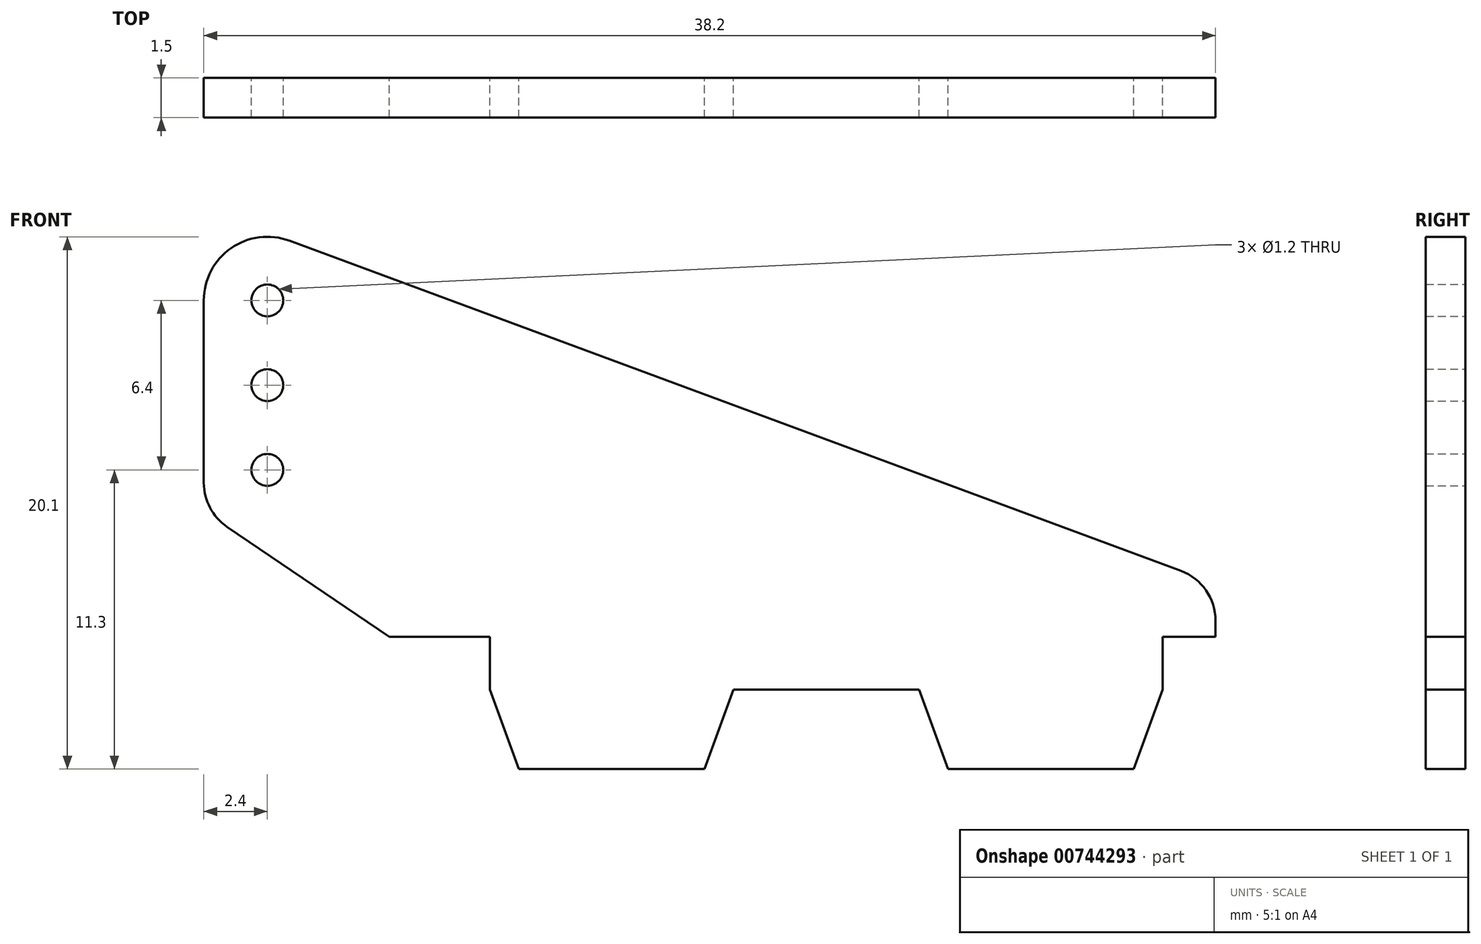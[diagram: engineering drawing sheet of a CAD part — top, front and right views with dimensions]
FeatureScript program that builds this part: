
annotation { "Feature Type Name" : "Feature", "Feature Type Description" : "" }
export const myFeature = defineFeature(function(context is Context, id is Id, definition is map)
    precondition{}
    {
        {
            var Q0;
            Q0=qCreatedBy(makeId("Front.planeOp"),FACE);
            var sketch = newSketch(context, id + "F0", { "sketchPlane" : qUnion([Q0])});
            skLineSegment(sketch, "E0", {"start": v(0, 0) * mm, "end": v(3.8, 0) * mm});
            skLineSegment(sketch, "E1", {"start": v(3.8, 0) * mm, "end": v(3.8, -2) * mm});
            skLineSegment(sketch, "E2", {"start": v(3.8, -2) * mm, "end": v(4.9, -5) * mm});
            skLineSegment(sketch, "E3", {"start": v(4.9, -5) * mm, "end": v(11.9, -5) * mm});
            skLineSegment(sketch, "E4", {"start": v(11.9, -5) * mm, "end": v(13, -2) * mm});
            skLineSegment(sketch, "E5", {"start": v(13, -2) * mm, "end": v(20, -2) * mm});
            skLineSegment(sketch, "E6", {"start": v(20, -2) * mm, "end": v(21.1, -5) * mm});
            skLineSegment(sketch, "E7", {"start": v(21.1, -5) * mm, "end": v(28.1, -5) * mm});
            skLineSegment(sketch, "E8", {"start": v(28.1, -5) * mm, "end": v(29.2, -2) * mm});
            skLineSegment(sketch, "E9", {"start": v(29.2, -2) * mm, "end": v(29.2, 0) * mm});
            skLineSegment(sketch, "E10", {"start": v(29.2, 0) * mm, "end": v(31.2, 0) * mm});
            skLineSegment(sketch, "E11", {"start": v(31.2, 0) * mm, "end": v(31.2, 0.6) * mm});
            skLineSegment(sketch, "E12", {"start": v(29.9, 2.48) * mm, "end": v(-3.77, 14.95) * mm});
            skLineSegment(sketch, "E13", {"start": v(0, 0) * mm, "end": v(-6.12, 4.15) * mm});
            skLineSegment(sketch, "E14", {"start": v(-7, 5.8) * mm, "end": v(-7, 12.7) * mm});
            skArc(sketch, "E15", {"start": v(-7, 12.7) * mm, "mid": v(-5.97, 14.67) * mm, "end": v(-3.77, 14.95) * mm});
            skCircle(sketch, "E16", {"center": v(-4.6, 12.7) * mm, "radius": 0.6 * mm});
            skPoint(sketch, "E17.visualSharp", {"position": v(31.2, 2) * mm});
            skArc(sketch, "E17.filletArc", {"start": v(31.2, 0.6) * mm, "mid": v(30.84, 1.75) * mm, "end": v(29.9, 2.48) * mm});
            skPoint(sketch, "E18.visualSharp", {"position": v(-7, 4.75) * mm});
            skArc(sketch, "E18.filletArc", {"start": v(-7, 5.8) * mm, "mid": v(-6.77, 4.87) * mm, "end": v(-6.12, 4.15) * mm});
            skCircle(sketch, "E19.0.1.0", {"center": v(-4.6, 9.5) * mm, "radius": 0.6 * mm});
            skCircle(sketch, "E19.0.2.0", {"center": v(-4.6, 6.3) * mm, "radius": 0.6 * mm});
            skLineSegment(sketch, "E19.direction1", {"start": v(-4.6, 12.7) * mm, "end": v(-29.6, 12.7) * mm, "construction": true});
            skLineSegment(sketch, "E19.direction2", {"start": v(-4.6, 12.7) * mm, "end": v(-4.6, 9.5) * mm, "construction": true});
            skLineSegment(sketch, "E20", {"start": v(26.13, 17.43) * mm, "end": v(22.33, 17.43) * mm});
            skLineSegment(sketch, "E21", {"start": v(22.33, 17.43) * mm, "end": v(22.33, 19.43) * mm});
            skLineSegment(sketch, "E22", {"start": v(22.33, 19.43) * mm, "end": v(21.24, 22.43) * mm});
            skLineSegment(sketch, "E23", {"start": v(21.24, 22.43) * mm, "end": v(14.23, 22.43) * mm});
            skLineSegment(sketch, "E24", {"start": v(14.23, 22.43) * mm, "end": v(13.13, 19.43) * mm});
            skLineSegment(sketch, "E25", {"start": v(13.13, 19.43) * mm, "end": v(6.12, 19.43) * mm});
            skLineSegment(sketch, "E26", {"start": v(6.12, 19.43) * mm, "end": v(5.03, 22.43) * mm});
            skLineSegment(sketch, "E27", {"start": v(5.03, 22.43) * mm, "end": v(-1.98, 22.43) * mm});
            skLineSegment(sketch, "E28", {"start": v(-1.98, 22.43) * mm, "end": v(-3.07, 19.43) * mm});
            skLineSegment(sketch, "E29", {"start": v(-3.07, 19.43) * mm, "end": v(-3.07, 17.43) * mm});
            skLineSegment(sketch, "E30", {"start": v(-3.07, 17.43) * mm, "end": v(-5.07, 17.43) * mm});
            skLineSegment(sketch, "E31", {"start": v(-5.07, 17.43) * mm, "end": v(-5.07, 16.83) * mm});
            skLineSegment(sketch, "E32", {"start": v(-3.77, 14.95) * mm, "end": v(29.9, 2.48) * mm});
            skLineSegment(sketch, "E33", {"start": v(26.13, 17.43) * mm, "end": v(32.25, 13.28) * mm});
            skLineSegment(sketch, "E34", {"start": v(33.13, 11.62) * mm, "end": v(33.13, 4.73) * mm});
            skArc(sketch, "E35", {"start": v(33.13, 4.73) * mm, "mid": v(32.1, 2.76) * mm, "end": v(29.9, 2.48) * mm});
            skCircle(sketch, "E36", {"center": v(30.73, 4.73) * mm, "radius": 0.6 * mm});
            skPoint(sketch, "E37.visualSharp", {"position": v(-5.07, 15.43) * mm});
            skArc(sketch, "E37.filletArc", {"start": v(-5.07, 16.83) * mm, "mid": v(-4.71, 15.68) * mm, "end": v(-3.77, 14.95) * mm});
            skPoint(sketch, "E38.visualSharp", {"position": v(33.13, 12.68) * mm});
            skArc(sketch, "E38.filletArc", {"start": v(33.13, 11.62) * mm, "mid": v(32.9, 12.56) * mm, "end": v(32.25, 13.28) * mm});
            skCircle(sketch, "E39.0.1.0", {"center": v(30.73, 7.93) * mm, "radius": 0.6 * mm});
            skCircle(sketch, "E39.0.2.0", {"center": v(30.73, 11.13) * mm, "radius": 0.6 * mm});
            skLineSegment(sketch, "E39.direction1", {"start": v(30.73, 4.73) * mm, "end": v(55.73, 4.73) * mm, "construction": true});
            skLineSegment(sketch, "E39.direction2", {"start": v(30.73, 4.73) * mm, "end": v(30.73, 7.93) * mm, "construction": true});
            skLineSegment(sketch, "E40", {"start": v(40.13, 0) * mm, "end": v(43.93, 0) * mm});
            skLineSegment(sketch, "E41", {"start": v(43.93, 0) * mm, "end": v(43.93, -2) * mm});
            skLineSegment(sketch, "E42", {"start": v(43.93, -2) * mm, "end": v(45.02, -5) * mm});
            skLineSegment(sketch, "E43", {"start": v(45.02, -5) * mm, "end": v(52.03, -5) * mm});
            skLineSegment(sketch, "E44", {"start": v(52.03, -5) * mm, "end": v(53.12, -2) * mm});
            skLineSegment(sketch, "E45", {"start": v(53.12, -2) * mm, "end": v(60.13, -2) * mm});
            skLineSegment(sketch, "E46", {"start": v(60.13, -2) * mm, "end": v(61.23, -5) * mm});
            skLineSegment(sketch, "E47", {"start": v(61.23, -5) * mm, "end": v(68.24, -5) * mm});
            skLineSegment(sketch, "E48", {"start": v(68.24, -5) * mm, "end": v(69.33, -2) * mm});
            skLineSegment(sketch, "E49", {"start": v(69.33, -2) * mm, "end": v(69.33, 0) * mm});
            skLineSegment(sketch, "E50", {"start": v(69.33, 0) * mm, "end": v(71.33, 0) * mm});
            skLineSegment(sketch, "E51", {"start": v(71.33, 0) * mm, "end": v(71.33, 0.6) * mm});
            skLineSegment(sketch, "E52", {"start": v(70.02, 2.48) * mm, "end": v(36.36, 14.95) * mm});
            skLineSegment(sketch, "E53", {"start": v(40.13, 0) * mm, "end": v(34, 4.15) * mm});
            skLineSegment(sketch, "E54", {"start": v(33.13, 5.8) * mm, "end": v(33.13, 12.7) * mm});
            skArc(sketch, "E55", {"start": v(33.13, 12.7) * mm, "mid": v(34.16, 14.67) * mm, "end": v(36.36, 14.95) * mm});
            skCircle(sketch, "E56", {"center": v(35.53, 12.7) * mm, "radius": 0.6 * mm});
            skPoint(sketch, "E57.visualSharp", {"position": v(71.33, 2) * mm});
            skArc(sketch, "E57.filletArc", {"start": v(71.33, 0.6) * mm, "mid": v(70.97, 1.75) * mm, "end": v(70.02, 2.48) * mm});
            skPoint(sketch, "E58.visualSharp", {"position": v(33.13, 4.75) * mm});
            skArc(sketch, "E58.filletArc", {"start": v(33.13, 5.8) * mm, "mid": v(33.36, 4.87) * mm, "end": v(34, 4.15) * mm});
            skCircle(sketch, "E59.0.1.0", {"center": v(35.53, 9.5) * mm, "radius": 0.6 * mm});
            skCircle(sketch, "E59.0.2.0", {"center": v(35.53, 6.3) * mm, "radius": 0.6 * mm});
            skLineSegment(sketch, "E59.direction1", {"start": v(35.53, 12.7) * mm, "end": v(10.53, 12.7) * mm, "construction": true});
            skLineSegment(sketch, "E59.direction2", {"start": v(35.53, 12.7) * mm, "end": v(35.53, 9.5) * mm, "construction": true});
            skLineSegment(sketch, "E60", {"start": v(66.26, 17.43) * mm, "end": v(62.46, 17.43) * mm});
            skLineSegment(sketch, "E61", {"start": v(62.46, 17.43) * mm, "end": v(62.46, 19.43) * mm});
            skLineSegment(sketch, "E62", {"start": v(62.46, 19.43) * mm, "end": v(61.36, 22.43) * mm});
            skLineSegment(sketch, "E63", {"start": v(61.36, 22.43) * mm, "end": v(54.35, 22.43) * mm});
            skLineSegment(sketch, "E64", {"start": v(54.35, 22.43) * mm, "end": v(53.26, 19.43) * mm});
            skLineSegment(sketch, "E65", {"start": v(53.26, 19.43) * mm, "end": v(46.25, 19.43) * mm});
            skLineSegment(sketch, "E66", {"start": v(46.25, 19.43) * mm, "end": v(45.16, 22.43) * mm});
            skLineSegment(sketch, "E67", {"start": v(45.16, 22.43) * mm, "end": v(38.15, 22.43) * mm});
            skLineSegment(sketch, "E68", {"start": v(38.15, 22.43) * mm, "end": v(37.06, 19.43) * mm});
            skLineSegment(sketch, "E69", {"start": v(37.06, 19.43) * mm, "end": v(37.06, 17.43) * mm});
            skLineSegment(sketch, "E70", {"start": v(37.06, 17.43) * mm, "end": v(35.06, 17.43) * mm});
            skLineSegment(sketch, "E71", {"start": v(35.06, 17.43) * mm, "end": v(35.06, 16.83) * mm});
            skLineSegment(sketch, "E72", {"start": v(36.36, 14.95) * mm, "end": v(70.02, 2.48) * mm});
            skLineSegment(sketch, "E73", {"start": v(66.26, 17.43) * mm, "end": v(72.38, 13.28) * mm});
            skLineSegment(sketch, "E74", {"start": v(73.26, 11.62) * mm, "end": v(73.26, 4.73) * mm});
            skArc(sketch, "E75", {"start": v(73.26, 4.73) * mm, "mid": v(72.23, 2.76) * mm, "end": v(70.02, 2.48) * mm});
            skCircle(sketch, "E76", {"center": v(70.86, 4.73) * mm, "radius": 0.6 * mm});
            skPoint(sketch, "E77.visualSharp", {"position": v(35.06, 15.43) * mm});
            skArc(sketch, "E77.filletArc", {"start": v(35.06, 16.83) * mm, "mid": v(35.41, 15.68) * mm, "end": v(36.36, 14.95) * mm});
            skPoint(sketch, "E78.visualSharp", {"position": v(73.26, 12.68) * mm});
            skArc(sketch, "E78.filletArc", {"start": v(73.26, 11.62) * mm, "mid": v(73.02, 12.56) * mm, "end": v(72.38, 13.28) * mm});
            skCircle(sketch, "E79.0.1.0", {"center": v(70.86, 7.93) * mm, "radius": 0.6 * mm});
            skCircle(sketch, "E79.0.2.0", {"center": v(70.86, 11.13) * mm, "radius": 0.6 * mm});
            skLineSegment(sketch, "E79.direction1", {"start": v(70.86, 4.73) * mm, "end": v(107.5, 4.73) * mm, "construction": true});
            skLineSegment(sketch, "E79.direction2", {"start": v(70.86, 4.73) * mm, "end": v(70.86, 7.93) * mm, "construction": true});
            skLineSegment(sketch, "E80", {"start": v(80.26, 0) * mm, "end": v(84.06, 0) * mm});
            skLineSegment(sketch, "E81", {"start": v(84.06, 0) * mm, "end": v(84.06, -2) * mm});
            skLineSegment(sketch, "E82", {"start": v(84.06, -2) * mm, "end": v(85.15, -5) * mm});
            skLineSegment(sketch, "E83", {"start": v(85.15, -5) * mm, "end": v(92.16, -5) * mm});
            skLineSegment(sketch, "E84", {"start": v(92.16, -5) * mm, "end": v(93.25, -2) * mm});
            skLineSegment(sketch, "E85", {"start": v(93.25, -2) * mm, "end": v(100.26, -2) * mm});
            skLineSegment(sketch, "E86", {"start": v(100.26, -2) * mm, "end": v(101.35, -5) * mm});
            skLineSegment(sketch, "E87", {"start": v(101.35, -5) * mm, "end": v(108.36, -5) * mm});
            skLineSegment(sketch, "E88", {"start": v(108.36, -5) * mm, "end": v(109.46, -2) * mm});
            skLineSegment(sketch, "E89", {"start": v(109.46, -2) * mm, "end": v(109.46, 0) * mm});
            skLineSegment(sketch, "E90", {"start": v(109.46, 0) * mm, "end": v(111.46, 0) * mm});
            skLineSegment(sketch, "E91", {"start": v(111.46, 0) * mm, "end": v(111.46, 0.6) * mm});
            skLineSegment(sketch, "E92", {"start": v(110.15, 2.48) * mm, "end": v(76.49, 14.95) * mm});
            skLineSegment(sketch, "E93", {"start": v(80.26, 0) * mm, "end": v(74.13, 4.15) * mm});
            skLineSegment(sketch, "E94", {"start": v(73.26, 5.8) * mm, "end": v(73.26, 12.7) * mm});
            skArc(sketch, "E95", {"start": v(73.26, 12.7) * mm, "mid": v(74.29, 14.67) * mm, "end": v(76.49, 14.95) * mm});
            skCircle(sketch, "E96", {"center": v(75.66, 12.7) * mm, "radius": 0.6 * mm});
            skPoint(sketch, "E97.visualSharp", {"position": v(111.46, 2) * mm});
            skArc(sketch, "E97.filletArc", {"start": v(111.46, 0.6) * mm, "mid": v(111.1, 1.75) * mm, "end": v(110.15, 2.48) * mm});
            skPoint(sketch, "E98.visualSharp", {"position": v(73.26, 4.75) * mm});
            skArc(sketch, "E98.filletArc", {"start": v(73.26, 5.8) * mm, "mid": v(73.49, 4.87) * mm, "end": v(74.13, 4.15) * mm});
            skCircle(sketch, "E99.0.1.0", {"center": v(75.66, 9.5) * mm, "radius": 0.6 * mm});
            skCircle(sketch, "E99.0.2.0", {"center": v(75.66, 6.3) * mm, "radius": 0.6 * mm});
            skLineSegment(sketch, "E99.direction1", {"start": v(75.66, 12.7) * mm, "end": v(50.66, 12.7) * mm, "construction": true});
            skLineSegment(sketch, "E99.direction2", {"start": v(75.66, 12.7) * mm, "end": v(75.66, 9.5) * mm, "construction": true});
            skLineSegment(sketch, "E100", {"start": v(106.38, 17.43) * mm, "end": v(102.58, 17.43) * mm});
            skLineSegment(sketch, "E101", {"start": v(102.58, 17.43) * mm, "end": v(102.58, 19.43) * mm});
            skLineSegment(sketch, "E102", {"start": v(102.58, 19.43) * mm, "end": v(101.5, 22.43) * mm});
            skLineSegment(sketch, "E103", {"start": v(101.5, 22.43) * mm, "end": v(94.48, 22.43) * mm});
            skLineSegment(sketch, "E104", {"start": v(94.48, 22.43) * mm, "end": v(93.39, 19.43) * mm});
            skLineSegment(sketch, "E105", {"start": v(93.39, 19.43) * mm, "end": v(86.38, 19.43) * mm});
            skLineSegment(sketch, "E106", {"start": v(86.38, 19.43) * mm, "end": v(85.29, 22.43) * mm});
            skLineSegment(sketch, "E107", {"start": v(85.29, 22.43) * mm, "end": v(78.28, 22.43) * mm});
            skLineSegment(sketch, "E108", {"start": v(78.28, 22.43) * mm, "end": v(77.18, 19.43) * mm});
            skLineSegment(sketch, "E109", {"start": v(77.18, 19.43) * mm, "end": v(77.18, 17.43) * mm});
            skLineSegment(sketch, "E110", {"start": v(77.18, 17.43) * mm, "end": v(75.18, 17.43) * mm});
            skLineSegment(sketch, "E111", {"start": v(75.18, 17.43) * mm, "end": v(75.18, 16.83) * mm});
            skLineSegment(sketch, "E112", {"start": v(76.49, 14.95) * mm, "end": v(110.15, 2.48) * mm});
            skLineSegment(sketch, "E113", {"start": v(106.38, 17.43) * mm, "end": v(112.5, 13.28) * mm});
            skLineSegment(sketch, "E114", {"start": v(113.38, 11.62) * mm, "end": v(113.38, 4.73) * mm});
            skArc(sketch, "E115", {"start": v(113.38, 4.73) * mm, "mid": v(112.36, 2.76) * mm, "end": v(110.15, 2.48) * mm});
            skCircle(sketch, "E116", {"center": v(110.98, 4.73) * mm, "radius": 0.6 * mm});
            skPoint(sketch, "E117.visualSharp", {"position": v(75.18, 15.43) * mm});
            skArc(sketch, "E117.filletArc", {"start": v(75.18, 16.83) * mm, "mid": v(75.54, 15.68) * mm, "end": v(76.49, 14.95) * mm});
            skPoint(sketch, "E118.visualSharp", {"position": v(113.38, 12.68) * mm});
            skArc(sketch, "E118.filletArc", {"start": v(113.38, 11.62) * mm, "mid": v(113.15, 12.56) * mm, "end": v(112.5, 13.28) * mm});
            skCircle(sketch, "E119.0.1.0", {"center": v(110.98, 7.93) * mm, "radius": 0.6 * mm});
            skCircle(sketch, "E119.0.2.0", {"center": v(110.98, 11.13) * mm, "radius": 0.6 * mm});
            skLineSegment(sketch, "E119.direction1", {"start": v(110.98, 4.73) * mm, "end": v(144.28, 4.73) * mm, "construction": true});
            skLineSegment(sketch, "E119.direction2", {"start": v(110.98, 4.73) * mm, "end": v(110.98, 7.93) * mm, "construction": true});
            skSolve(sketch);
        }
        {
            var Q0;
            Q0=makeQuery(id+"F0.imprint","IMPRINT",FACE,{"disambiguationData":[TD([[makeQuery(id+"F0.imprint","IMPRINT",EDGE,{"derivedFrom":sQuery(id+"F0.wireOp",EDGE,"E0")}),1.0]])]});
            extrude(context, id + "F1", {"entities" : qUnion([Q0]), "depth" : 1.5 * mm});
        }
    });
